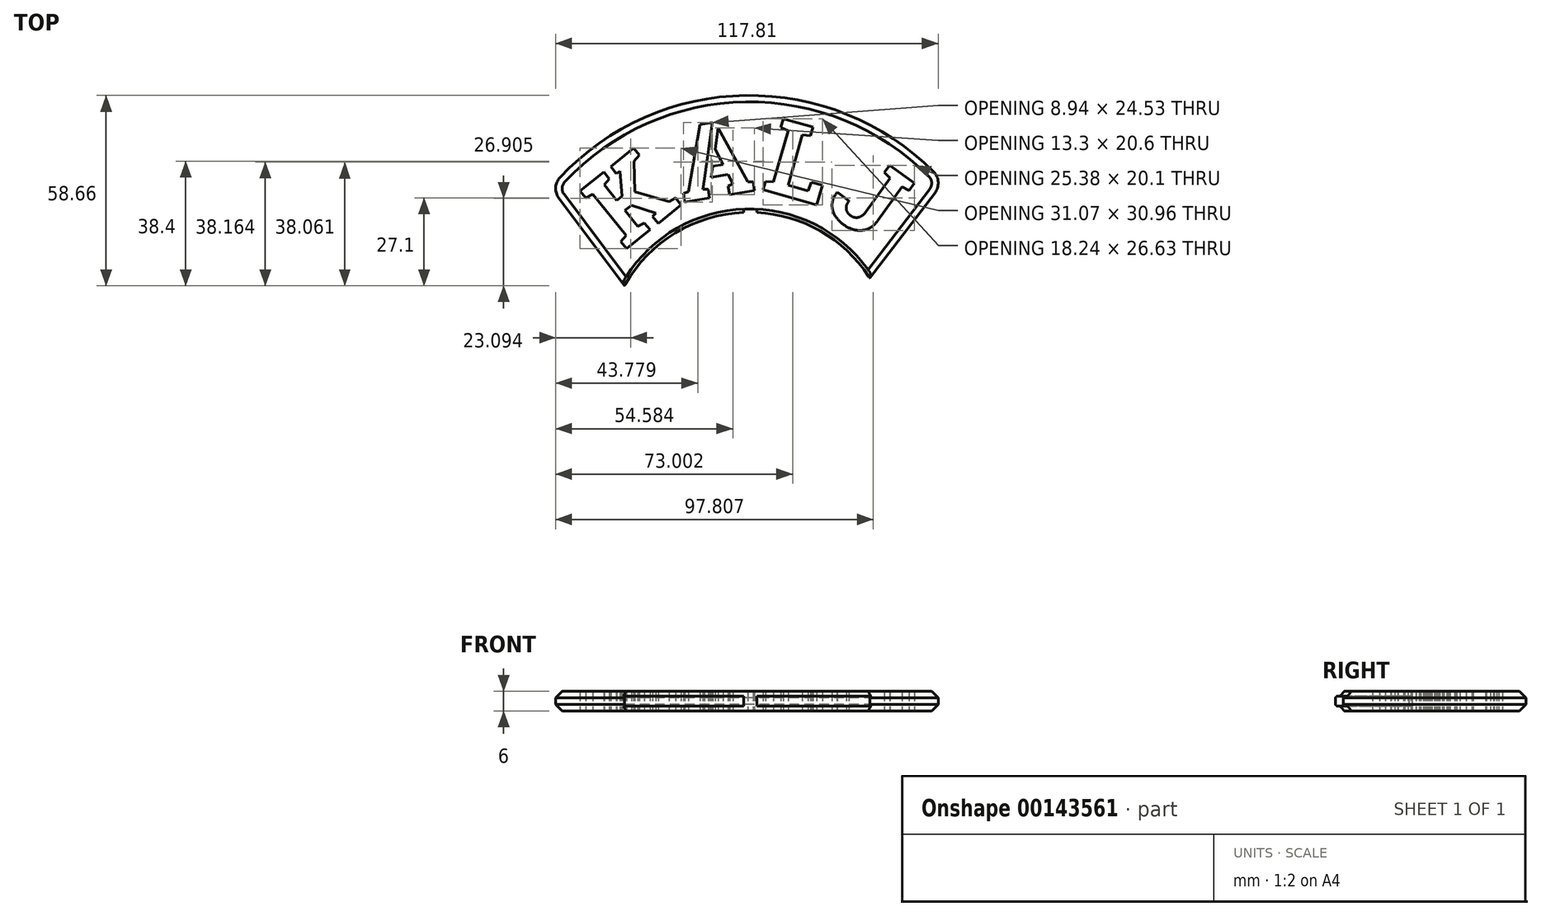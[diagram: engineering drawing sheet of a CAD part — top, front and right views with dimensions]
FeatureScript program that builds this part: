
annotation { "Feature Type Name" : "Feature", "Feature Type Description" : "" }
export const myFeature = defineFeature(function(context is Context, id is Id, definition is map)
    precondition{}
    {
        {
            var Q0;
            Q0=qCreatedBy(makeId("Top.planeOp"),FACE);
            var sketch = newSketch(context, id + "F0", { "sketchPlane" : qUnion([Q0])});
            skCircle(sketch, "E0", {"center": v(0, 0) * mm, "radius": 50 * mm, "construction": true});
            skText(sketch, "E1", { "text": "L", "fontName": "RobotoSlab-Bold.ttf"});
            skText(sketch, "E2", { "text": "K", "fontName": "RobotoSlab-Bold.ttf"});
            skText(sketch, "E3", { "text": "A", "fontName": "RobotoSlab-Bold.ttf"});
            skText(sketch, "E4", { "text": "J", "fontName": "RobotoSlab-Bold.ttf"});
            skArc(sketch, "E5.0", {"start": v(37.7, 24.57) * mm, "mid": v(-1.38, 44.98) * mm, "end": v(-39.13, 22.22) * mm});
            skArc(sketch, "E6", {"start": v(59.68, 53.28) * mm, "mid": v(-1.12, 80) * mm, "end": v(-61.14, 51.6) * mm});
            skLineSegment(sketch, "E7", {"start": v(0, 0) * mm, "end": v(-41.65, 55.6) * mm, "construction": true});
            skLineSegment(sketch, "E8", {"start": v(0, 0) * mm, "end": v(44.37, 57.96) * mm, "construction": true});
            skLineSegment(sketch, "E9.0", {"start": v(37.05, 23.73) * mm, "end": v(59.68, 53.28) * mm});
            skLineSegment(sketch, "E10.0", {"start": v(-38.48, 21.34) * mm, "end": v(-61.14, 51.6) * mm});
            skArc(sketch, "E11.0", {"start": v(37.05, 23.73) * mm, "mid": v(22.09, 38.05) * mm, "end": v(2.23, 43.94) * mm});
            skLineSegment(sketch, "E12", {"start": v(0.23, 44) * mm, "end": v(0.23, 45) * mm, "construction": true});
            skLineSegment(sketch, "E13.0", {"start": v(-1.77, 43.96) * mm, "end": v(-1.77, 44.97) * mm});
            skLineSegment(sketch, "E14.0", {"start": v(2.23, 43.94) * mm, "end": v(2.23, 44.94) * mm});
            skArc(sketch, "E15.trimOffspring", {"start": v(-1.77, 43.96) * mm, "mid": v(-23.09, 37.46) * mm, "end": v(-38.48, 21.34) * mm});
            skLineSegment(sketch, "E16.bottom", {"start": v(-11.14, 73.88) * mm, "end": v(-9.16, 73.6) * mm});
            skLineSegment(sketch, "E16.top", {"start": v(-13.87, 54.07) * mm, "end": v(-11.89, 53.8) * mm});
            skLineSegment(sketch, "E16.left", {"start": v(-11.14, 73.88) * mm, "end": v(-13.87, 54.07) * mm});
            skLineSegment(sketch, "E16.right", {"start": v(-9.16, 73.6) * mm, "end": v(-11.89, 53.8) * mm});
            const initialGuessF0  = {"E1": [0.00335, 0.05114, 0.9615, -0.27482, 0.02309], "E2": [-0.0386, 0.03222, 0.7817, 0.62364, 0.02309], "E3": [-0.02056, 0.04703, 0.98636, 0.16457, 0.02309], "E4": [0.0227, 0.04508, 0.8129, -0.5824, 0.02309]};
            skSetInitialGuess(sketch, initialGuessF0);
            skSolve(sketch);
        }
        {
            var Q0;
            Q0=makeQuery(id+"F0.imprint","IMPRINT",FACE,{"disambiguationData":[TD([[makeQuery(id+"F0.imprint","IMPRINT",EDGE,{"derivedFrom":sQuery(id+"F0.wireOp",EDGE,"E1.sketch_text.stroke-0")}),1.0]])]});
            var Q1;
            Q1=makeQuery(id+"F0.imprint","IMPRINT",FACE,{"disambiguationData":[TD([[makeQuery(id+"F0.imprint","IMPRINT",EDGE,{"derivedFrom":sQuery(id+"F0.wireOp",EDGE,"E3.sketch_text.stroke-16")}),1.0]])]});
            var Q2;
            {var subQ0=sQuery(id+"F0.wireOp",EDGE,"E16.right");var subQ1=sQuery(id+"F0.wireOp",EDGE,"E3.sketch_text.stroke-10");var subQ2=makeQuery(id+"F0.imprint","INTERSECT",VERTEX,{"derivedFrom":[subQ1,subQ0]});Q2=makeQuery(id+"F0.imprint","IMPRINT",FACE,{"disambiguationData":[TD([[makeQuery(id+"F0.imprint","IMPRINT",EDGE,{"disambiguationData":[TD([[subQ2,-1.0]])],"derivedFrom":subQ1}),-1.0]])]});}
            var Q3;
            {var subQ5=sQuery(id+"F0.wireOp",EDGE,"E16.bottom");Q3=makeQuery(id+"F0.imprint","IMPRINT",FACE,{"disambiguationData":[TD([[makeQuery(id+"F0.imprint","IMPRINT",EDGE,{"derivedFrom":subQ5}),-1.0]])]});}
            var Q4;
            {var subQ5=sQuery(id+"F0.wireOp",EDGE,"E16.top");Q4=makeQuery(id+"F0.imprint","IMPRINT",FACE,{"disambiguationData":[TD([[makeQuery(id+"F0.imprint","IMPRINT",EDGE,{"derivedFrom":subQ5}),1.0]])]});}
            var Q5;
            {var subQ1=sQuery(id+"F0.wireOp",EDGE,"E3.sketch_text.stroke-18");Q5=makeQuery(id+"F0.imprint","IMPRINT",FACE,{"disambiguationData":[TD([[makeQuery(id+"F0.imprint","IMPRINT",EDGE,{"derivedFrom":subQ1}),1.0]])]});}
            var Q6;
            {var subQ6=sQuery(id+"F0.wireOp",EDGE,"E3.sketch_text.stroke-18");Q6=makeQuery(id+"F0.imprint","IMPRINT",FACE,{"disambiguationData":[TD([[makeQuery(id+"F0.imprint","IMPRINT",EDGE,{"derivedFrom":subQ6}),-1.0]])]});}
            extrude(context, id + "F1", {"entities" : qUnion([Q0, Q1, Q2, Q3, Q4, Q5, Q6]), "endBound" : BoundingType.SYMMETRIC, "depth" : 6 * mm});
        }
        {
            var Q0;
            {var subQ3=sQuery(id+"F0.wireOp",EDGE,"E13.0");Q0=makeQuery(id+"F0.imprint","IMPRINT",FACE,{"disambiguationData":[TD([[makeQuery(id+"F0.imprint","IMPRINT",EDGE,{"derivedFrom":subQ3}),1.0]])]});}
            var Q1;
            {var subQ4=sQuery(id+"F0.wireOp",EDGE,"E11.0");Q1=makeQuery(id+"F0.imprint","IMPRINT",FACE,{"disambiguationData":[TD([[makeQuery(id+"F0.imprint","IMPRINT",EDGE,{"derivedFrom":subQ4}),-1.0]])]});}
            extrude(context, id + "F2", {"entities" : qUnion([Q0, Q1]), "operationType" : NewBodyOperationType.ADD, "endBound" : BoundingType.SYMMETRIC, "depth" : 3 * mm});
        }
        {
            var Q0;
            Q0=makeQuery(id+"F1.opExtrude","SWEPT_EDGE",EDGE,{"disambiguationData":[OSD([sQuery(id+"F0.wireOp",EDGE,"E6"),sQuery(id+"F0.wireOp",EDGE,"E9.0")])]});
            var Q1;
            Q1=makeQuery(id+"F1.opExtrude","SWEPT_EDGE",EDGE,{"disambiguationData":[OSD([sQuery(id+"F0.wireOp",EDGE,"E6"),sQuery(id+"F0.wireOp",EDGE,"E10.0")])]});
            fillet(context, id + "F3", {"entities" : qUnion([Q0, Q1]), "radius" : 5 * mm, "tangentPropagation" : true, "allowEdgeOverflow" : false});
        }
        {
            var Q0;
            Q0=makeQuery(id+"F1.opExtrude","CAP_EDGE",EDGE,{"disambiguationData":[OSD([sQuery(id+"F0.wireOp",EDGE,"E6")])],"isStart":false});
            var Q1;
            Q1=makeQuery(id+"F1.opExtrude","CAP_EDGE",EDGE,{"disambiguationData":[OSD([sQuery(id+"F0.wireOp",EDGE,"E6")])],"isStart":true});
            chamfer(context, id + "F4", {"entities" : qUnion([Q0, Q1]), "width" : 2 * mm, "tangentPropagation" : true});
        }
    });
